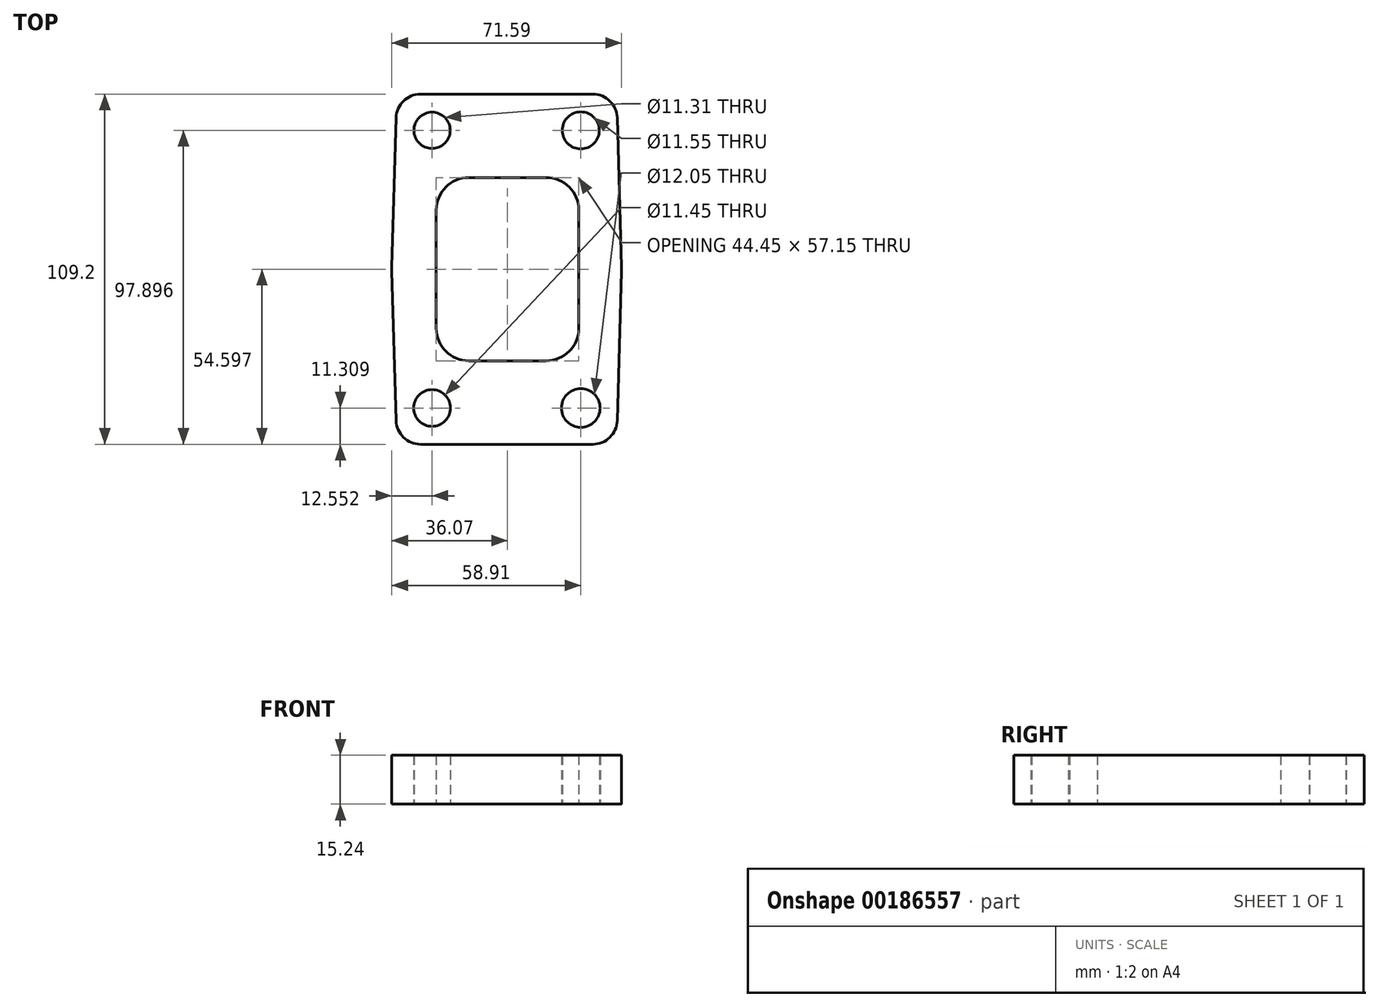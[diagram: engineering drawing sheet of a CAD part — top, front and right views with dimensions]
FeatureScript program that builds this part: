
annotation { "Feature Type Name" : "Feature", "Feature Type Description" : "" }
export const myFeature = defineFeature(function(context is Context, id is Id, definition is map)
    precondition{}
    {
        {
            var Q0;
            Q0=qCreatedBy(makeId("Top.planeOp"),FACE);
            var sketch = newSketch(context, id + "F0", { "sketchPlane" : qUnion([Q0])});
            skCircle(sketch, "E0", {"center": v(-130.02, -2.58) * mm, "radius": 6.03 * mm});
            skCircle(sketch, "E1", {"center": v(-130.02, 84) * mm, "radius": 5.77 * mm});
            skCircle(sketch, "E2", {"center": v(-176.38, 84) * mm, "radius": 5.65 * mm});
            skCircle(sketch, "E3", {"center": v(-176.38, -2.58) * mm, "radius": 5.73 * mm});
            skLineSegment(sketch, "E4", {"start": v(-130.64, 22.3) * mm, "end": v(-130.64, 59.12) * mm});
            skLineSegment(sketch, "E5", {"start": v(-140.8, 12.13) * mm, "end": v(-164.93, 12.13) * mm});
            skLineSegment(sketch, "E6", {"start": v(-175.09, 22.3) * mm, "end": v(-175.09, 59.12) * mm});
            skLineSegment(sketch, "E7", {"start": v(-164.93, 69.28) * mm, "end": v(-140.8, 69.28) * mm});
            skLineSegment(sketch, "E8", {"start": v(-179.97, 95.31) * mm, "end": v(-126.27, 95.31) * mm});
            skLineSegment(sketch, "E9", {"start": v(-118.65, 87.9) * mm, "end": v(-117.33, 40.71) * mm});
            skLineSegment(sketch, "E10", {"start": v(-117.33, 40.71) * mm, "end": v(-118.65, -6.48) * mm});
            skLineSegment(sketch, "E11", {"start": v(-126.27, -13.89) * mm, "end": v(-179.97, -13.89) * mm});
            skLineSegment(sketch, "E12", {"start": v(-187.6, -6.49) * mm, "end": v(-188.94, 40.71) * mm});
            skLineSegment(sketch, "E13", {"start": v(-188.94, 40.71) * mm, "end": v(-187.6, 87.91) * mm});
            skArc(sketch, "E14", {"start": v(-187.6, -6.49) * mm, "mid": v(-185.28, -11.73) * mm, "end": v(-179.97, -13.89) * mm});
            skArc(sketch, "E15", {"start": v(-126.27, -13.89) * mm, "mid": v(-120.96, -11.73) * mm, "end": v(-118.65, -6.48) * mm});
            skArc(sketch, "E16", {"start": v(-140.8, 12.13) * mm, "mid": v(-133.61, 15.1) * mm, "end": v(-130.64, 22.3) * mm});
            skArc(sketch, "E17", {"start": v(-175.09, 22.3) * mm, "mid": v(-172.1, 15.1) * mm, "end": v(-164.93, 12.13) * mm});
            skArc(sketch, "E18", {"start": v(-164.93, 69.28) * mm, "mid": v(-172.1, 66.3) * mm, "end": v(-175.09, 59.12) * mm});
            skArc(sketch, "E19", {"start": v(-130.64, 59.12) * mm, "mid": v(-133.61, 66.3) * mm, "end": v(-140.8, 69.28) * mm});
            skArc(sketch, "E20", {"start": v(-118.65, 87.9) * mm, "mid": v(-120.96, 93.16) * mm, "end": v(-126.27, 95.31) * mm});
            skArc(sketch, "E21", {"start": v(-179.97, 95.31) * mm, "mid": v(-185.28, 93.16) * mm, "end": v(-187.6, 87.91) * mm});
            skSolve(sketch);
        }
        {
            var Q0;
            Q0=makeQuery(id+"F0.imprint","IMPRINT",FACE,{"disambiguationData":[TD([[makeQuery(id+"F0.imprint","IMPRINT",EDGE,{"derivedFrom":sQuery(id+"F0.wireOp",EDGE,"E0")}),-1.0]])]});
            extrude(context, id + "F1", {"entities" : qUnion([Q0]), "depth" : 15.24 * mm});
        }
        {
            var Q0;
            Q0=makeQuery(id+"F1.opExtrude","SWEPT_EDGE",EDGE,{"disambiguationData":[OSD([sQuery(id+"F0.wireOp",EDGE,"E9"),sQuery(id+"F0.wireOp",EDGE,"E10")])]});
            var Q1;
            Q1=makeQuery(id+"F1.opExtrude","SWEPT_EDGE",EDGE,{"disambiguationData":[OSD([sQuery(id+"F0.wireOp",EDGE,"E12"),sQuery(id+"F0.wireOp",EDGE,"E13")])]});
            fillet(context, id + "F2", {"entities" : qUnion([Q0, Q1]), "radius" : 25.4 * mm, "tangentPropagation" : true, "allowEdgeOverflow" : false});
        }
    });
